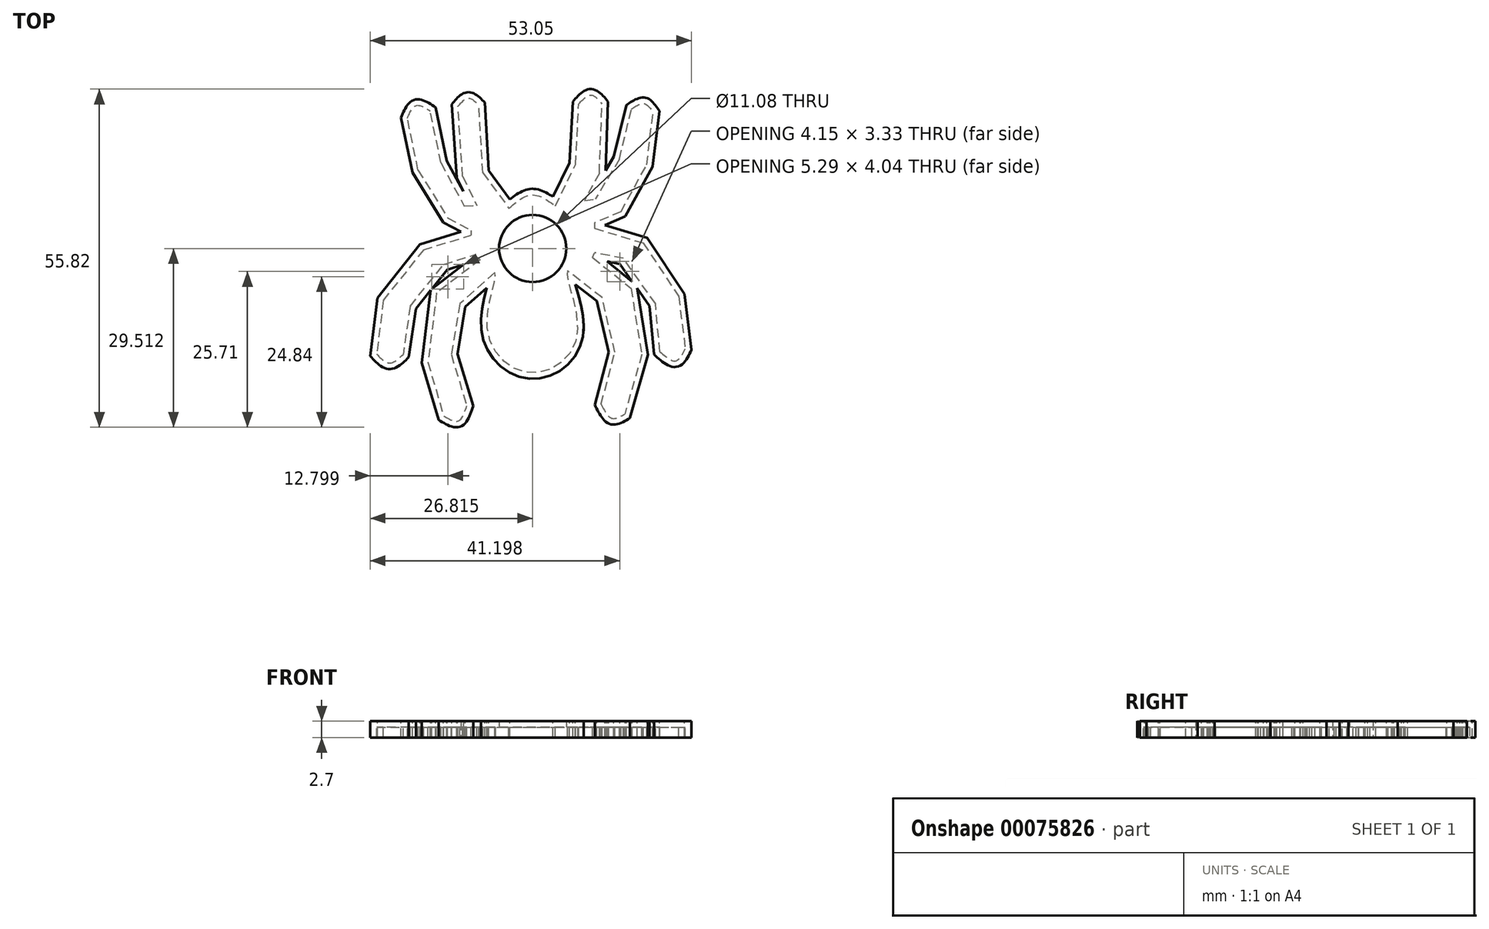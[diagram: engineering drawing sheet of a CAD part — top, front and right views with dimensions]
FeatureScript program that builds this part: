
annotation { "Feature Type Name" : "Feature", "Feature Type Description" : "" }
export const myFeature = defineFeature(function(context is Context, id is Id, definition is map)
    precondition{}
    {
        {
            var Q0;
            Q0=qCreatedBy(makeId("Top.planeOp"),FACE);
            var sketch = newSketch(context, id + "F0", { "sketchPlane" : qUnion([Q0])});
            skLineSegment(sketch, "E0", {"start": v(20.13, 43.3) * mm, "end": v(19.46, 54.46) * mm});
            skLineSegment(sketch, "E1", {"start": v(16.8, 42.73) * mm, "end": v(16, 54.27) * mm});
            skLineSegment(sketch, "E2", {"start": v(9.43, 43.77) * mm, "end": v(7.67, 52.31) * mm});
            skLineSegment(sketch, "E3", {"start": v(13.2, 44.95) * mm, "end": v(11.44, 53.5) * mm});
            skLineSegment(sketch, "E4", {"start": v(13.2, 44.95) * mm, "end": v(17.05, 37.84) * mm});
            skLineSegment(sketch, "E5", {"start": v(9.43, 43.77) * mm, "end": v(14.32, 35.89) * mm});
            skLineSegment(sketch, "E6", {"start": v(20.13, 43.3) * mm, "end": v(24.42, 37.45) * mm});
            skLineSegment(sketch, "E7", {"start": v(16.8, 42.73) * mm, "end": v(19.14, 37.9) * mm});
            skLineSegment(sketch, "E8", {"start": v(10.34, 30.6) * mm, "end": v(18.16, 33.02) * mm});
            skLineSegment(sketch, "E9", {"start": v(10.34, 30.6) * mm, "end": v(3.7, 22.27) * mm});
            skLineSegment(sketch, "E10", {"start": v(3.7, 22.27) * mm, "end": v(2.58, 13.4) * mm});
            skLineSegment(sketch, "E11", {"start": v(8.12, 21.29) * mm, "end": v(13.66, 28.2) * mm});
            skLineSegment(sketch, "E12", {"start": v(13.66, 28.2) * mm, "end": v(18.7, 29.75) * mm});
            skLineSegment(sketch, "E13", {"start": v(14.32, 35.89) * mm, "end": v(18.16, 33.8) * mm});
            skLineSegment(sketch, "E14", {"start": v(18.16, 33.8) * mm, "end": v(18.16, 33.02) * mm});
            skLineSegment(sketch, "E15", {"start": v(32.1, 37.84) * mm, "end": v(35.43, 44.69) * mm});
            skLineSegment(sketch, "E16", {"start": v(35.43, 44.69) * mm, "end": v(35.94, 54.66) * mm});
            skLineSegment(sketch, "E17", {"start": v(39.35, 43.25) * mm, "end": v(39.79, 54.7) * mm});
            skLineSegment(sketch, "E18", {"start": v(39.35, 43.25) * mm, "end": v(36.9, 38.71) * mm});
            skLineSegment(sketch, "E19", {"start": v(42.67, 45.57) * mm, "end": v(44.68, 53.87) * mm});
            skLineSegment(sketch, "E20", {"start": v(42.67, 45.57) * mm, "end": v(38.7, 38.97) * mm});
            skLineSegment(sketch, "E21", {"start": v(42.93, 36.92) * mm, "end": v(47.17, 44.6) * mm});
            skLineSegment(sketch, "E22", {"start": v(47.17, 44.6) * mm, "end": v(48.22, 53.26) * mm});
            skLineSegment(sketch, "E23", {"start": v(42.93, 36.92) * mm, "end": v(38.55, 35.05) * mm});
            skLineSegment(sketch, "E24", {"start": v(38.55, 35.05) * mm, "end": v(38.55, 34.14) * mm});
            skLineSegment(sketch, "E25", {"start": v(38.55, 34.14) * mm, "end": v(46.62, 31.71) * mm});
            skLineSegment(sketch, "E26", {"start": v(46.62, 31.71) * mm, "end": v(52.45, 22.93) * mm});
            skLineSegment(sketch, "E27", {"start": v(52.45, 22.93) * mm, "end": v(53.55, 14.27) * mm});
            skLineSegment(sketch, "E28", {"start": v(49.33, 13.8) * mm, "end": v(48.63, 21.69) * mm});
            skLineSegment(sketch, "E29", {"start": v(48.63, 21.69) * mm, "end": v(43.32, 29.18) * mm});
            skLineSegment(sketch, "E30", {"start": v(43.32, 29.18) * mm, "end": v(38.56, 30.12) * mm});
            skLineSegment(sketch, "E31", {"start": v(38.25, 29.34) * mm, "end": v(44.57, 24.26) * mm});
            skLineSegment(sketch, "E32", {"start": v(44.57, 24.26) * mm, "end": v(46.36, 13.33) * mm});
            skLineSegment(sketch, "E33", {"start": v(46.36, 13.33) * mm, "end": v(43.55, 3.5) * mm});
            skLineSegment(sketch, "E34", {"start": v(39.65, 5.13) * mm, "end": v(41.91, 13.72) * mm});
            skLineSegment(sketch, "E35", {"start": v(41.91, 13.72) * mm, "end": v(39.8, 22.7) * mm});
            skLineSegment(sketch, "E36", {"start": v(39.8, 22.7) * mm, "end": v(34.1, 27.15) * mm});
            skLineSegment(sketch, "E37", {"start": v(38.25, 29.34) * mm, "end": v(38.56, 30.12) * mm});
            skLineSegment(sketch, "E38", {"start": v(18.7, 29.75) * mm, "end": v(19.67, 28.97) * mm});
            skPoint(sketch, "E38.endSnap0", {"position": v(16.18, 28.97) * mm});
            skLineSegment(sketch, "E39", {"start": v(19.67, 28.97) * mm, "end": v(12.48, 23.48) * mm});
            skLineSegment(sketch, "E40", {"start": v(12.48, 23.48) * mm, "end": v(11.08, 12) * mm});
            skLineSegment(sketch, "E41", {"start": v(11.08, 12) * mm, "end": v(13.65, 3.18) * mm});
            skLineSegment(sketch, "E42", {"start": v(22.08, 26.84) * mm, "end": v(16.3, 21.69) * mm});
            skLineSegment(sketch, "E43", {"start": v(16.3, 21.69) * mm, "end": v(14.9, 13.33) * mm});
            skLineSegment(sketch, "E44", {"start": v(14.9, 13.33) * mm, "end": v(17.48, 4.82) * mm});
            skFitSpline(sketch, "E45", {"points": [v(13.65, 3.18) * mm, v(16.05, 2.36) * mm, v(17.48, 4.82) * mm], "startDerivative": vector(5.47, -3.26) * mm, "endDerivative": vector(2.21, 6.45) * mm});
            skFitSpline(sketch, "E46", {"points": [v(39.65, 5.13) * mm, v(41.43, 2.8) * mm, v(43.55, 3.5) * mm], "startDerivative": vector(3.01, -5.94) * mm, "endDerivative": vector(4.84, 2.87) * mm});
            skFitSpline(sketch, "E47", {"points": [v(49.33, 13.8) * mm, v(51.95, 12.27) * mm, v(53.55, 14.27) * mm], "startDerivative": vector(5.46, -4.79) * mm, "endDerivative": vector(2.93, 5.87) * mm});
            skFitSpline(sketch, "E48", {"points": [v(44.68, 53.87) * mm, v(46.75, 54.71) * mm, v(48.22, 53.26) * mm], "startDerivative": vector(4.33, 2.83) * mm, "endDerivative": vector(2.73, -4.1) * mm});
            skFitSpline(sketch, "E49", {"points": [v(35.94, 54.66) * mm, v(37.96, 56.13) * mm, v(39.79, 54.7) * mm], "startDerivative": vector(4.02, 4.39) * mm, "endDerivative": vector(3.66, -4.35) * mm});
            skFitSpline(sketch, "E50", {"points": [v(16, 54.27) * mm, v(17.74, 55.63) * mm, v(19.46, 54.46) * mm], "startDerivative": vector(3.38, 3.96) * mm, "endDerivative": vector(3.53, -3.6) * mm});
            skFitSpline(sketch, "E51", {"points": [v(7.67, 52.31) * mm, v(9.1, 54.4) * mm, v(11.44, 53.5) * mm], "startDerivative": vector(2.39, 5.68) * mm, "endDerivative": vector(5.16, -3.29) * mm});
            skLineSegment(sketch, "E52", {"start": v(8.12, 21.29) * mm, "end": v(6.96, 13.35) * mm});
            skFitSpline(sketch, "E53", {"points": [v(2.58, 13.4) * mm, v(4.73, 11.92) * mm, v(6.96, 13.35) * mm], "startDerivative": vector(4.27, -4.41) * mm, "endDerivative": vector(4.49, 4.29) * mm});
            skFitSpline(sketch, "E54", {"points": [v(34.1, 27.15) * mm, v(34.1, 25.85) * mm, v(35.52, 15.79) * mm, v(27.9, 10.3) * mm, v(20.99, 16.7) * mm, v(22.08, 25.54) * mm, v(22.08, 26.84) * mm], "startDerivative": vector(-2.57, -12.08) * mm, "endDerivative": vector(-2.2, 12.54) * mm});
            skFitSpline(sketch, "E55", {"points": [v(17.05, 37.84) * mm, v(19.14, 37.9) * mm], "startDerivative": vector(2.09, 0.07) * mm, "endDerivative": vector(2.09, 0.07) * mm});
            skFitSpline(sketch, "E56", {"points": [v(24.42, 37.45) * mm, v(28.2, 39.67) * mm, v(32.1, 37.84) * mm], "startDerivative": vector(7.46, 6.45) * mm, "endDerivative": vector(7.92, -5.69) * mm});
            skFitSpline(sketch, "E57", {"points": [v(36.9, 38.71) * mm, v(38.7, 38.97) * mm], "startDerivative": vector(1.8, 0.26) * mm, "endDerivative": vector(1.8, 0.26) * mm});
            skSolve(sketch);
        }
        {
            var Q0;
            Q0=makeQuery(id+"F0.imprint","IMPRINT",FACE,{"disambiguationData":[TD([[makeQuery(id+"F0.imprint","IMPRINT",EDGE,{"derivedFrom":sQuery(id+"F0.wireOp",EDGE,"E0")}),1.0]])]});
            extrude(context, id + "F1", {"entities" : qUnion([Q0]), "oppositeDirection" : true, "depth" : 1.7 * mm});
        }
        {
            var Q0;
            Q0=makeQuery(id+"F1.opExtrude","CAP_FACE",FACE,{"disambiguationData":[OSD([sQuery(id+"F0.wireOp",EDGE,"E0"),sQuery(id+"F0.wireOp",EDGE,"E1"),sQuery(id+"F0.wireOp",EDGE,"E2"),sQuery(id+"F0.wireOp",EDGE,"E3"),sQuery(id+"F0.wireOp",EDGE,"E4"),sQuery(id+"F0.wireOp",EDGE,"E5"),sQuery(id+"F0.wireOp",EDGE,"E6"),sQuery(id+"F0.wireOp",EDGE,"E7"),sQuery(id+"F0.wireOp",EDGE,"E8"),sQuery(id+"F0.wireOp",EDGE,"E9"),sQuery(id+"F0.wireOp",EDGE,"E10"),sQuery(id+"F0.wireOp",EDGE,"E11"),sQuery(id+"F0.wireOp",EDGE,"E12"),sQuery(id+"F0.wireOp",EDGE,"E13"),sQuery(id+"F0.wireOp",EDGE,"E14"),sQuery(id+"F0.wireOp",EDGE,"E15"),sQuery(id+"F0.wireOp",EDGE,"E16"),sQuery(id+"F0.wireOp",EDGE,"E17"),sQuery(id+"F0.wireOp",EDGE,"E18"),sQuery(id+"F0.wireOp",EDGE,"E19"),sQuery(id+"F0.wireOp",EDGE,"E20"),sQuery(id+"F0.wireOp",EDGE,"E21"),sQuery(id+"F0.wireOp",EDGE,"E22"),sQuery(id+"F0.wireOp",EDGE,"E23"),sQuery(id+"F0.wireOp",EDGE,"E24"),sQuery(id+"F0.wireOp",EDGE,"E25"),sQuery(id+"F0.wireOp",EDGE,"E26"),sQuery(id+"F0.wireOp",EDGE,"E27"),sQuery(id+"F0.wireOp",EDGE,"E28"),sQuery(id+"F0.wireOp",EDGE,"E29"),sQuery(id+"F0.wireOp",EDGE,"E30"),sQuery(id+"F0.wireOp",EDGE,"E31"),sQuery(id+"F0.wireOp",EDGE,"E32"),sQuery(id+"F0.wireOp",EDGE,"E33"),sQuery(id+"F0.wireOp",EDGE,"E34"),sQuery(id+"F0.wireOp",EDGE,"E35"),sQuery(id+"F0.wireOp",EDGE,"E36"),sQuery(id+"F0.wireOp",EDGE,"E37"),sQuery(id+"F0.wireOp",EDGE,"E38"),sQuery(id+"F0.wireOp",EDGE,"E39"),sQuery(id+"F0.wireOp",EDGE,"E40"),sQuery(id+"F0.wireOp",EDGE,"E41"),sQuery(id+"F0.wireOp",EDGE,"E42"),sQuery(id+"F0.wireOp",EDGE,"E43"),sQuery(id+"F0.wireOp",EDGE,"E44"),sQuery(id+"F0.wireOp",EDGE,"E45"),sQuery(id+"F0.wireOp",EDGE,"E46"),sQuery(id+"F0.wireOp",EDGE,"E47"),sQuery(id+"F0.wireOp",EDGE,"E48"),sQuery(id+"F0.wireOp",EDGE,"E49"),sQuery(id+"F0.wireOp",EDGE,"E50"),sQuery(id+"F0.wireOp",EDGE,"E51"),sQuery(id+"F0.wireOp",EDGE,"E52"),sQuery(id+"F0.wireOp",EDGE,"E53"),sQuery(id+"F0.wireOp",EDGE,"E54"),sQuery(id+"F0.wireOp",EDGE,"E55"),sQuery(id+"F0.wireOp",EDGE,"E56"),sQuery(id+"F0.wireOp",EDGE,"E57")])],"isStart":false});
            shell(context, id + "F2", {"entities" : qUnion([Q0]), "thickness" : 1 * mm, "oppositeDirection" : true});
        }
        {
            var Q0;
            Q0=makeQuery(id+"F2.opShell","OFFSET_FACE",FACE,{"disambiguationData":[OSD([sQuery(id+"F0.wireOp",EDGE,"E0"),sQuery(id+"F0.wireOp",EDGE,"E1"),sQuery(id+"F0.wireOp",EDGE,"E2"),sQuery(id+"F0.wireOp",EDGE,"E3"),sQuery(id+"F0.wireOp",EDGE,"E4"),sQuery(id+"F0.wireOp",EDGE,"E5"),sQuery(id+"F0.wireOp",EDGE,"E6"),sQuery(id+"F0.wireOp",EDGE,"E7"),sQuery(id+"F0.wireOp",EDGE,"E8"),sQuery(id+"F0.wireOp",EDGE,"E9"),sQuery(id+"F0.wireOp",EDGE,"E10"),sQuery(id+"F0.wireOp",EDGE,"E11"),sQuery(id+"F0.wireOp",EDGE,"E12"),sQuery(id+"F0.wireOp",EDGE,"E13"),sQuery(id+"F0.wireOp",EDGE,"E14"),sQuery(id+"F0.wireOp",EDGE,"E15"),sQuery(id+"F0.wireOp",EDGE,"E16"),sQuery(id+"F0.wireOp",EDGE,"E17"),sQuery(id+"F0.wireOp",EDGE,"E18"),sQuery(id+"F0.wireOp",EDGE,"E19"),sQuery(id+"F0.wireOp",EDGE,"E20"),sQuery(id+"F0.wireOp",EDGE,"E21"),sQuery(id+"F0.wireOp",EDGE,"E22"),sQuery(id+"F0.wireOp",EDGE,"E23"),sQuery(id+"F0.wireOp",EDGE,"E24"),sQuery(id+"F0.wireOp",EDGE,"E25"),sQuery(id+"F0.wireOp",EDGE,"E26"),sQuery(id+"F0.wireOp",EDGE,"E27"),sQuery(id+"F0.wireOp",EDGE,"E28"),sQuery(id+"F0.wireOp",EDGE,"E29"),sQuery(id+"F0.wireOp",EDGE,"E30"),sQuery(id+"F0.wireOp",EDGE,"E31"),sQuery(id+"F0.wireOp",EDGE,"E32"),sQuery(id+"F0.wireOp",EDGE,"E33"),sQuery(id+"F0.wireOp",EDGE,"E34"),sQuery(id+"F0.wireOp",EDGE,"E35"),sQuery(id+"F0.wireOp",EDGE,"E36"),sQuery(id+"F0.wireOp",EDGE,"E37"),sQuery(id+"F0.wireOp",EDGE,"E38"),sQuery(id+"F0.wireOp",EDGE,"E39"),sQuery(id+"F0.wireOp",EDGE,"E40"),sQuery(id+"F0.wireOp",EDGE,"E41"),sQuery(id+"F0.wireOp",EDGE,"E42"),sQuery(id+"F0.wireOp",EDGE,"E43"),sQuery(id+"F0.wireOp",EDGE,"E44"),sQuery(id+"F0.wireOp",EDGE,"E45"),sQuery(id+"F0.wireOp",EDGE,"E46"),sQuery(id+"F0.wireOp",EDGE,"E47"),sQuery(id+"F0.wireOp",EDGE,"E48"),sQuery(id+"F0.wireOp",EDGE,"E49"),sQuery(id+"F0.wireOp",EDGE,"E50"),sQuery(id+"F0.wireOp",EDGE,"E51"),sQuery(id+"F0.wireOp",EDGE,"E52"),sQuery(id+"F0.wireOp",EDGE,"E53"),sQuery(id+"F0.wireOp",EDGE,"E54"),sQuery(id+"F0.wireOp",EDGE,"E55"),sQuery(id+"F0.wireOp",EDGE,"E56"),sQuery(id+"F0.wireOp",EDGE,"E57")])]});
            var sketch = newSketch(context, id + "F3", { "sketchPlane" : qUnion([Q0])});
            skCircle(sketch, "E58", {"center": v(28.35, -30.82) * mm, "radius": 5.54 * mm});
            skSolve(sketch);
        }
        {
            var Q0;
            Q0=makeQuery(id+"F3.imprint","IMPRINT",FACE,{"disambiguationData":[TD([[makeQuery(id+"F3.imprint","IMPRINT",EDGE,{"derivedFrom":sQuery(id+"F3.wireOp",EDGE,"E58")}),1.0]])]});
            extrude(context, id + "F4", {"entities" : qUnion([Q0]), "operationType" : NewBodyOperationType.REMOVE, "oppositeDirection" : true, "depth" : 5 * mm});
        }
    });
